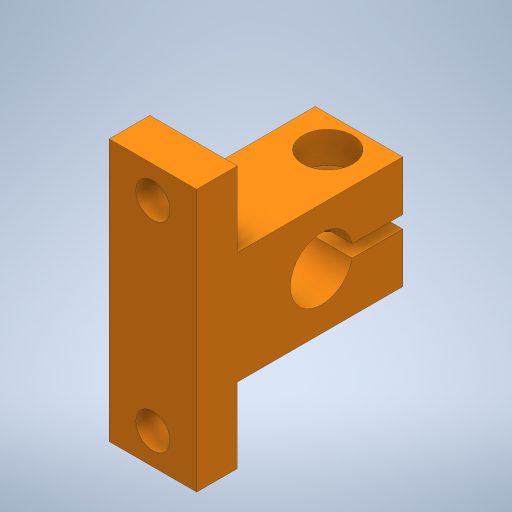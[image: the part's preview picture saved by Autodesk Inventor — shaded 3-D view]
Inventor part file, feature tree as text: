
AUTODESK INVENTOR PART (.ipt)
format: ipt  version: 2023 (Build 270158000, 158)  size: 276,480 bytes
history: native  units: mm
features: extrude x1, sketch x1
ambient origin geometry x8: Origin, YZ Plane, XZ Plane, XY Plane, X Axis, Y Axis, Z Axis, Center Point
bodies: Solid2 (feature_tree), Solid1 (feature_tree)
feature tree (2):
  extrude  "Extrusion1"  Depth=20.0mm TaperAngle=0.0deg
  sketch  "Sketch1"  dims[d0=10.0mm d1=20.0mm d2=0.0mm]
